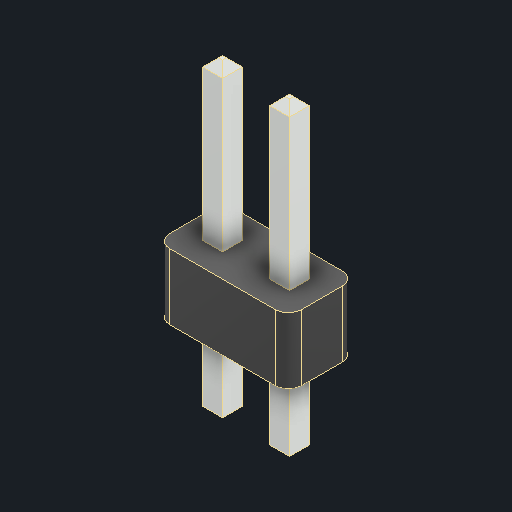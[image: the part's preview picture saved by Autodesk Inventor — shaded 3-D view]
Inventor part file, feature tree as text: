
AUTODESK INVENTOR PART (.ipt)
format: ipt  version: 2023 (Build 270158000, 158)  size: 118,784 bytes
history: native  units: in
note: dims shown in document units (in); Inventor stores cm internally (conversion verified against a paired STEP export)
features: chamfer x1
ambient origin geometry x8: Origin, YZ Plane, XZ Plane, XY Plane, X Axis, Y Axis, Z Axis, Center Point
bodies: Solid1 (feature_tree)
feature tree (1):
  chamfer  "Chamfer1"  [1 undecoded]
note: 1 required parameter value undecoded (feature->parameter linkage not recoverable at this tier; creation-order binding heuristic only, values carry confidence <= 0.55)
